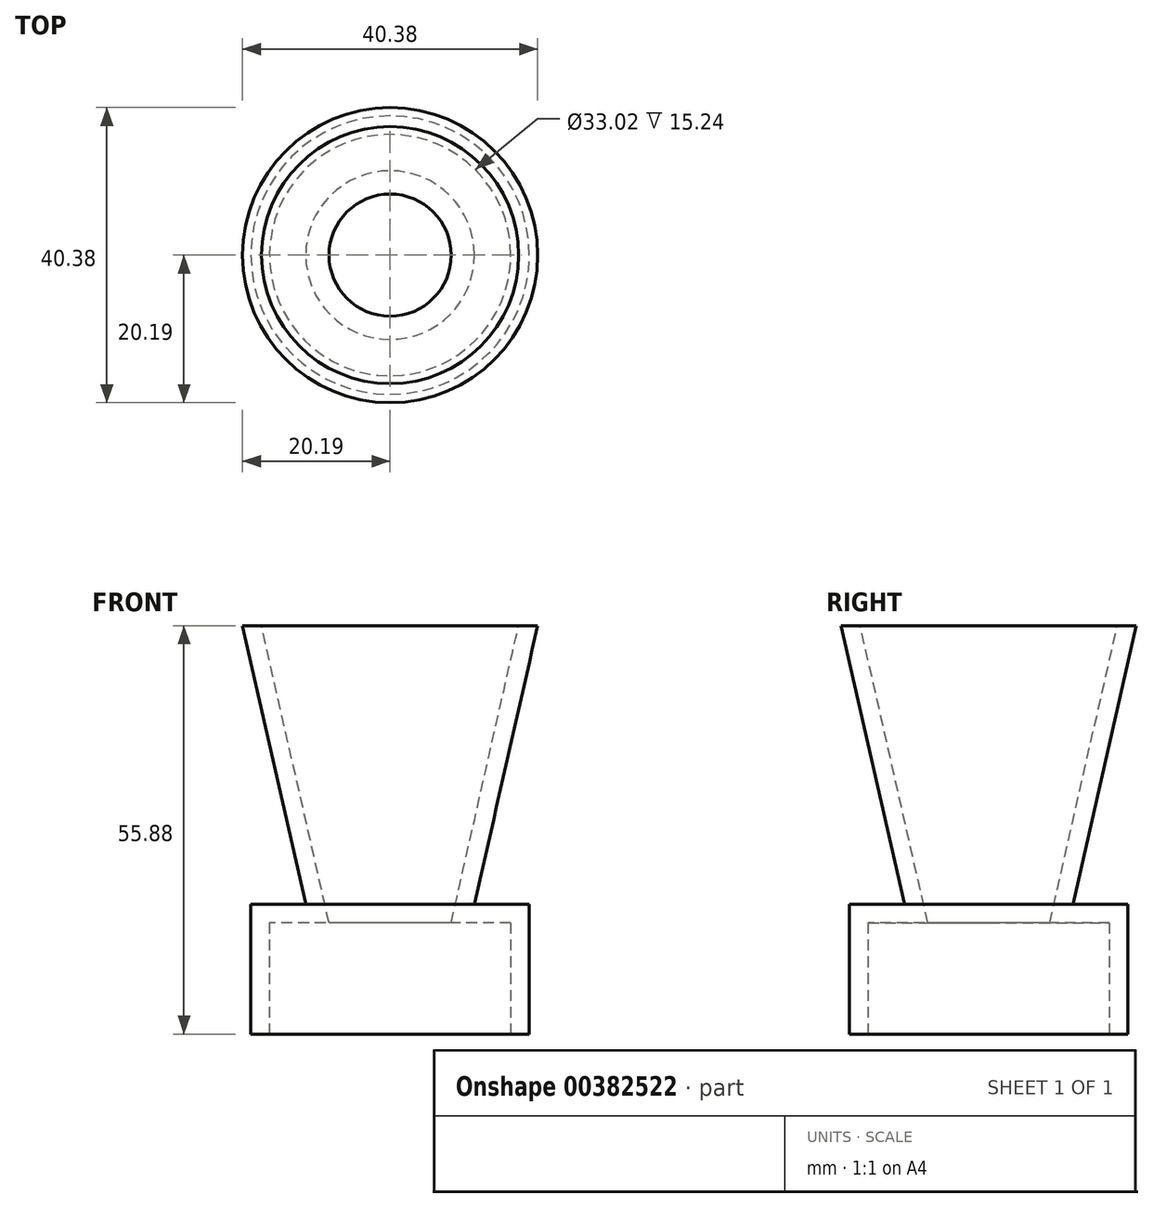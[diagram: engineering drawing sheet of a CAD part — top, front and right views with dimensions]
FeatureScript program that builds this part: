
annotation { "Feature Type Name" : "Feature", "Feature Type Description" : "" }
export const myFeature = defineFeature(function(context is Context, id is Id, definition is map)
    precondition{}
    {
        {
            var Q0;
            Q0=qCreatedBy(makeId("Top.planeOp"),FACE);
            var sketch = newSketch(context, id + "F0", { "sketchPlane" : qUnion([Q0])});
            skCircle(sketch, "E0", {"center": v(0, 0) * mm, "radius": 19.05 * mm});
            skSolve(sketch);
        }
        {
            var Q0;
            Q0=makeQuery(id+"F0.imprint","IMPRINT",FACE,{"disambiguationData":[TD([[makeQuery(id+"F0.imprint","IMPRINT",EDGE,{"derivedFrom":sQuery(id+"F0.wireOp",EDGE,"E0")}),1.0]])]});
            extrude(context, id + "F1", {"entities" : qUnion([Q0]), "depth" : 17.78 * mm});
        }
        {
            var Q0;
            Q0=makeQuery(id+"F1.opExtrude","CAP_FACE",FACE,{"disambiguationData":[OSD([sQuery(id+"F0.wireOp",EDGE,"E0")])],"isStart":false});
            cPlane(context, id + "F2", {"entities" : qUnion([Q0]), "cplaneType" : CPlaneType.OFFSET, "offset" : 38.1 * mm, "width" : 152.4 * mm, "height" : 152.4 * mm});
        }
        {
            var Q0;
            Q0=qCreatedBy(id+"F2.planeOp",FACE);
            var sketch = newSketch(context, id + "F3", { "sketchPlane" : qUnion([Q0])});
            skCircle(sketch, "E1", {"center": v(0, 0) * mm, "radius": 20.19 * mm});
            skSolve(sketch);
        }
        {
            var Q0;
            Q0=makeQuery(id+"F1.opExtrude","CAP_FACE",FACE,{"disambiguationData":[OSD([sQuery(id+"F0.wireOp",EDGE,"E0")])],"isStart":false});
            var sketch = newSketch(context, id + "F4", { "sketchPlane" : qUnion([Q0])});
            skCircle(sketch, "E2", {"center": v(0, 0) * mm, "radius": 11.54 * mm});
            skSolve(sketch);
        }
        {
            var Q1;
            Q1=makeQuery(id+"F4.imprint","IMPRINT",FACE,{"disambiguationData":[TD([[makeQuery(id+"F4.imprint","IMPRINT",EDGE,{"derivedFrom":sQuery(id+"F4.wireOp",EDGE,"E2")}),1.0]])]});
            var Q2;
            Q2=makeQuery(id+"F3.imprint","IMPRINT",FACE,{"disambiguationData":[TD([[makeQuery(id+"F3.imprint","IMPRINT",EDGE,{"derivedFrom":sQuery(id+"F3.wireOp",EDGE,"E1")}),1.0]])]});
            loft(context, id + "F5", {"operationType" : NewBodyOperationType.ADD, "sheetProfilesArray" : [{ "sheetProfileEntities" : qUnion([Q1]) }, { "sheetProfileEntities" : qUnion([Q2]) }]});
        }
        {
            var Q0;
            Q0=makeQuery(id+"F1.opExtrude","CAP_FACE",FACE,{"disambiguationData":[OSD([sQuery(id+"F0.wireOp",EDGE,"E0")])],"isStart":true});
            var Q1;
            Q1=makeQuery(id+"F5.opLoft","CAP_FACE",FACE,{"disambiguationData":[OSD([makeQuery(id+"F3.imprint","IMPRINT",FACE,{"disambiguationData":[TD([[makeQuery(id+"F3.imprint","IMPRINT",EDGE,{"derivedFrom":sQuery(id+"F3.wireOp",EDGE,"E1")}),1.0]])]})])],"isStart":true});
            shell(context, id + "F6", {"entities" : qUnion([Q0, Q1]), "thickness" : 2.54 * mm});
        }
    });
